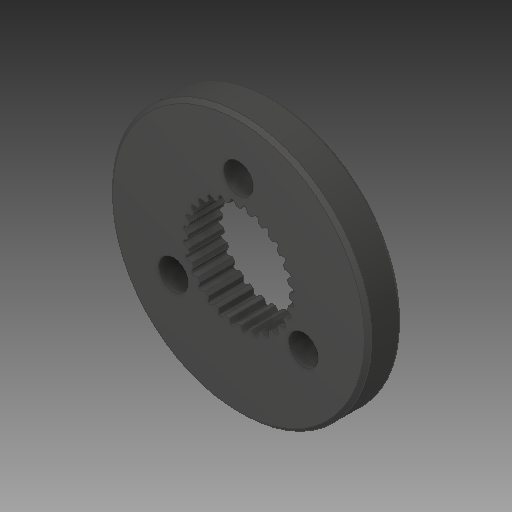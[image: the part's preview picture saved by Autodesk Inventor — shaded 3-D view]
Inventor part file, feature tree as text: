
AUTODESK INVENTOR PART (.ipt)
format: ipt  version: 2017 (Build 210142000, 142)  size: 265,728 bytes
history: native  units: in
note: dims shown in document units (in); Inventor stores cm internally (conversion verified against a paired STEP export)
features: chamfer x1
ambient origin geometry x8: Origin, YZ Plane, XZ Plane, XY Plane, X Axis, Y Axis, Z Axis, Center Point
bodies: Solid1 (feature_tree)
feature tree (1):
  chamfer  "Chamfer1"  [1 undecoded]
note: 1 required parameter value undecoded (feature->parameter linkage not recoverable at this tier; creation-order binding heuristic only, values carry confidence <= 0.55)
